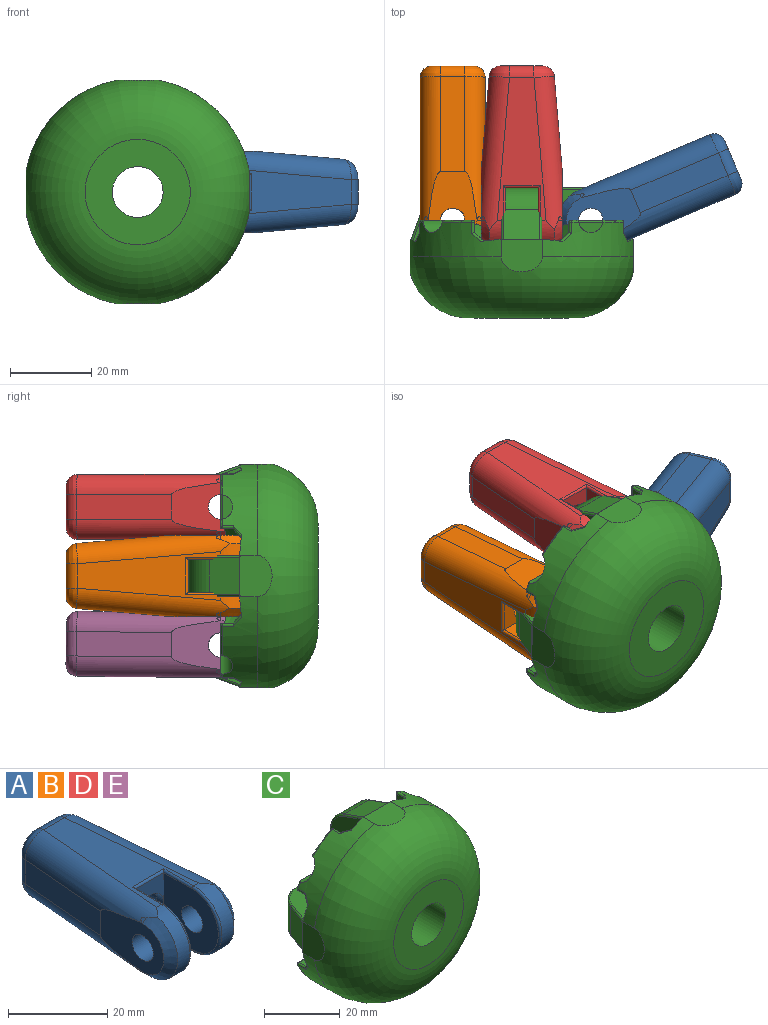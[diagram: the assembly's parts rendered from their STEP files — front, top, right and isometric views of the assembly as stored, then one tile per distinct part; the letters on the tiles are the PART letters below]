
ASSEMBLY  parts=5 mates=4
PART A: 43 faces, bbox 22.4x46.7x17.3 mm
  f0: plane 35.2x12mm, normal (0,0,1), area 240mm2, adj f1,f4,f25,f27,f29,f32,f34,f35
  f1: cylinder r=8mm len=16mm, axis (-1,0,0), area 82mm2, adj f0,f2,f18,f23,f31,f34
  f2: plane 35.2x12mm, normal (0,0,-1), area 240mm2, adj f1,f4,f22,f24,f26,f31,f33,f42
  f3: cylinder r=3mm len=6mm, axis (-1,0,0), area 112.2mm2, adj f8,f10
  f4: cylinder r=8mm len=16mm, axis (-1,0,0), area 82mm2, adj f0,f2,f15,f28,f32,f33
  f5: plane 10.45x10.4mm, normal (0,1,0), area 22.8mm2, adj f20,f35,f36,f37,f38,f39,f40,f41
  f6: cylinder r=3mm len=6mm, axis (-1,0,0), area 112.2mm2, adj f7,f11
  f7: plane 18x12mm, normal (1,0,0), area 149.6mm2, adj f6,f12,f14,f15,f16,f32,f33
  f8: plane 18x12mm, normal (-1,0,0), area 149.6mm2, adj f3,f13,f17,f18,f19,f31,f34
  f9: plane 15x8.1mm, normal (0,-1,0), area 71.2mm2, adj f10,f11,f24,f27,f30
  f10: plane 15.5x15mm, normal (1,0,0), area 180.1mm2, adj f3,f9,f22,f23,f25
  f11: plane 15.5x15mm, normal (-1,0,0), area 180.1mm2, adj f6,f9,f26,f28,f29
  f12: plane 23.44x6mm, normal (1,0.08,0), area 141.1mm2, adj f7,f32,f33,f38
  f13: plane 23.44x6mm, normal (-1,0.08,0), area 141.1mm2, adj f8,f31,f34,f39
  f14: plane 1.02x1.02mm, normal (0.71,0,-0.71), area 1mm2, adj f7,f15,f33
  f15: cone r=6mm half-angle=45deg, axis (-1,0,0), area 58.7mm2, adj f4,f7,f14,f16,f32,f33
  f16: plane 1.02x1.02mm, normal (0.71,0,0.71), area 1mm2, adj f7,f15,f32
  f17: plane 1.02x1.02mm, normal (-0.71,0,-0.71), area 1mm2, adj f8,f18,f31
  f18: cone r=8mm half-angle=45deg, axis (1,0,0), area 58.7mm2, adj f1,f8,f17,f19,f31,f34
  f19: plane 1.02x1.02mm, normal (-0.71,0,0.71), area 1mm2, adj f8,f18,f34
  f20: cylinder r=5.1mm len=28mm, axis (0,1,0), area 897.2mm2, adj f5,f21
  f21: plane 10.2x10.2mm, normal (0,1,0), area 31.4mm2, adj f20,f30
  f22: cylinder r=0.5mm len=8.5mm, axis (0,1,0), area 6.4mm2, adj f2,f10,f23,f24
  f23: torus R=7.5mm, axis (1,0,0), area 19.3mm2, adj f1,f10,f22,f25
  f24: cylinder r=0.5mm len=9.1mm, axis (1,0,0), area 6.6mm2, adj f2,f9,f22,f26
  f25: cylinder r=0.5mm len=8.5mm, axis (0,-1,0), area 6.4mm2, adj f0,f10,f23,f27
  f26: cylinder r=0.5mm len=8.5mm, axis (0,-1,0), area 6.4mm2, adj f2,f11,f24,f28
  f27: cylinder r=0.5mm len=9.1mm, axis (-1,0,0), area 6.6mm2, adj f0,f9,f25,f29
  f28: torus R=7.5mm, axis (1,0,0), area 19.3mm2, adj f4,f11,f26,f29
  f29: cylinder r=0.5mm len=8.5mm, axis (0,1,0), area 6.4mm2, adj f0,f11,f27,f28
  f30: cylinder r=4mm len=8mm, axis (0,1,0), area 50.3mm2, adj f9,f21
  f31: cylinder r=5mm len=38.07mm, axis (0.08,1,0), area 255.8mm2, adj f1,f2,f8,f13,f17,f18,f41
  f32: cylinder r=5mm len=38.07mm, axis (-0.08,1,0), area 255.8mm2, adj f0,f4,f7,f12,f15,f16,f36
  f33: cylinder r=5mm len=38.07mm, axis (-0.08,1,0), area 255.8mm2, adj f2,f4,f7,f12,f14,f15,f40
  f34: cylinder r=5mm len=38.07mm, axis (0.08,1,0), area 255.8mm2, adj f0,f1,f8,f13,f18,f19,f37
  f35: cylinder r=2.8mm len=6.04mm, axis (1,0,0), area 26.6mm2, adj f0,f5,f36,f37
  f36: bspline ~5.88x5.22mm, area 26.4mm2, adj f5,f32,f35,f38
  f37: bspline ~5.87x5.23mm, area 26.4mm2, adj f5,f34,f35,f39
  f38: cylinder r=2.8mm len=6mm, axis (0,0,1), area 25mm2, adj f5,f12,f36,f40
  f39: cylinder r=2.8mm len=6mm, axis (0,0,1), area 25mm2, adj f5,f13,f37,f41
  f40: bspline ~5.87x5.23mm, area 26.4mm2, adj f5,f33,f38,f42
  f41: bspline ~5.88x5.22mm, area 26.4mm2, adj f5,f31,f39,f42
  f42: cylinder r=2.8mm len=6.04mm, axis (-1,0,0), area 26.6mm2, adj f2,f5,f40,f41
PART B: same geometry as A
PART C: 170 faces, bbox 58.4x35.2x58.6 mm
  f0: plane 12.55x1.9mm, normal (0,1,0), area 22.9mm2, adj f2,f113,f115,f169
  f1: cylinder r=0.5mm len=4.69mm, axis (1,0,0), area 3.7mm2, adj f54,f74,f114,f169
  f2: torus R=27.46mm, axis (0,-1,0), area 1.6mm2, adj f0,f19,f117,f169
  f3: plane 12.55x1.9mm, normal (0,1,0), area 22.9mm2, adj f4,f123,f125,f168
  f4: torus R=27.46mm, axis (0,-1,0), area 1.6mm2, adj f3,f28,f122,f168
  f5: cylinder r=0.5mm len=4.69mm, axis (0,0,-1), area 3.7mm2, adj f45,f75,f126,f168
  f6: plane 12.55x1.9mm, normal (0,1,0), area 22.9mm2, adj f96,f97,f98,f167
  f7: torus R=27.46mm, axis (0,-1,0), area 6.7mm2, adj f33,f76,f99,f167
  f8: cylinder r=0.5mm len=4.69mm, axis (-1,0,0), area 3.7mm2, adj f39,f76,f99,f167
  f9: plane 12.55x1.9mm, normal (0,1,0), area 22.9mm2, adj f104,f106,f107,f166
  f10: cylinder r=0.5mm len=4.69mm, axis (0,0,1), area 3.7mm2, adj f63,f73,f105,f166
  f11: torus R=27.46mm, axis (0,-1,0), area 6.7mm2, adj f20,f73,f105,f166
  f12: plane 7.75x5.04mm, normal (0,0.94,0.34), area 28.4mm2, adj f27,f28,f77,f128,f146,f147
  f13: plane 7.57x4.05mm, normal (0,0.01,1), area 30.4mm2, adj f15,f24,f71,f135,f137
  f14: plane 20.38x7.85mm, normal (0,0.94,-0.34), area 67.6mm2, adj f15,f19,f20,f21,f65,f68,f70,f71
  f15: cylinder r=8mm len=10.74mm, axis (-1,0,0), area 63.4mm2, adj f13,f14,f23,f71,f87
  f16: plane 7.57x4.05mm, normal (1,0.01,0), area 30.4mm2, adj f17,f62,f66,f140,f141
  f17: cylinder r=8mm len=10.74mm, axis (0,0,1), area 63.4mm2, adj f16,f25,f62,f65,f83
  f18: plane 34x34mm, normal (0,1,0), area 466.8mm2, adj f37,f40,f49,f58,f67,f134,f135,f136
  f19: cylinder r=27.96mm len=22.45mm, axis (0,1,0), area 207.8mm2, adj f2,f14,f21,f25,f29,f72,f111,f112
  f20: cylinder r=27.96mm len=22.45mm, axis (0,1,0), area 207.8mm2, adj f11,f14,f21,f35,f36,f72,f102,f103
  f21: plane 10.1x8mm, normal (0,0,1), area 72.8mm2, adj f14,f19,f20,f72
  f22: plane 13.05x5mm, normal (0,0,-1), area 51.1mm2, adj f63,f85,f86,f106,f109,f110
  f23: cylinder r=8mm len=10.74mm, axis (0,0,-1), area 63.4mm2, adj f15,f24,f35,f43,f86
  f24: plane 7.57x4.05mm, normal (-1,0.01,0), area 30.4mm2, adj f13,f23,f43,f134,f136
  f25: plane 20.38x7.85mm, normal (-0.34,0.94,0), area 67.6mm2, adj f17,f19,f28,f29,f56,f59,f61,f62
  f26: plane 7.57x4.05mm, normal (0,0.01,-1), area 30.4mm2, adj f27,f53,f57,f150,f151
  f27: cylinder r=8mm len=10.74mm, axis (1,0,0), area 63.5mm2, adj f12,f26,f53,f56,f78,f129,f146
  f28: cylinder r=27.96mm len=22.45mm, axis (0,1,0), area 208.1mm2, adj f4,f12,f25,f29,f34,f72,f120,f121
  f29: plane 10.1x8mm, normal (1,0,0), area 72.8mm2, adj f19,f25,f28,f72
  f30: plane 14.04x7.85mm, normal (0,0.94,0.34), area 34.8mm2, adj f33,f34,f47,f50,f52,f92,f93,f147
  f31: plane 7.57x4.05mm, normal (-1,0.01,0), area 30.4mm2, adj f32,f44,f48,f158,f159
  f32: cylinder r=8mm len=10.74mm, axis (0,0,-1), area 63.4mm2, adj f31,f35,f44,f47,f90
  f33: cylinder r=27.96mm len=22.45mm, axis (0,1,0), area 207.8mm2, adj f7,f30,f34,f35,f36,f72,f93,f94
  f34: plane 12.6x10.55mm, normal (0,0,-1), area 72.8mm2, adj f28,f30,f33,f72,f147
  f35: plane 20.38x7.85mm, normal (0.34,0.94,0), area 67.6mm2, adj f20,f23,f32,f33,f36,f41,f43,f44
  f36: plane 10.1x8mm, normal (-1,0,0), area 72.8mm2, adj f20,f33,f35,f72
  f37: cylinder r=6.25mm len=32mm, axis (0,1,0), area 1256.6mm2, adj f18,f38
  f38: plane 25.92x25.92mm, normal (0,-1,0), area 404.9mm2, adj f37,f72
  f39: plane 13.05x5mm, normal (0,0,1), area 39.9mm2, adj f8,f46,f89,f90,f98,f100,f101,f167
  f40: cylinder r=8mm len=8.9mm, axis (0,0,-1), area 87mm2, adj f18,f41,f132,f157
  f41: plane 8.9x7.52mm, normal (-0.94,0.34,0), area 71.2mm2, adj f35,f40,f130,f156
  f42: cylinder r=3mm len=9.9mm, axis (0,0,-1), area 186.6mm2, adj f43,f44
  f43: plane 17.85x15.5mm, normal (0,0,1), area 187.8mm2, adj f23,f24,f35,f42,f130,f132,f134
  f44: plane 17.85x15.5mm, normal (0,0,-1), area 187.8mm2, adj f31,f32,f35,f42,f156,f157,f158
  f45: plane 12.58x5.03mm, normal (-1,0,0), area 39.2mm2, adj f5,f77,f78,f125,f127,f128,f129,f164
  f46: plane 13.05x5mm, normal (1,0,0), area 51.1mm2, adj f39,f91,f92,f93,f94,f96
  f47: cylinder r=8mm len=10.74mm, axis (1,0,0), area 63.4mm2, adj f30,f32,f48,f52,f91
  f48: plane 7.57x4.05mm, normal (0,0.01,-1), area 30.4mm2, adj f31,f47,f52,f160,f161
  f49: cylinder r=8mm len=8.9mm, axis (1,0,0), area 87mm2, adj f18,f50,f149,f163
  f50: plane 8.9x7.52mm, normal (0,0.34,-0.94), area 71.1mm2, adj f30,f49,f147,f148,f162
  f51: cylinder r=3mm len=9.9mm, axis (1,0,0), area 186.6mm2, adj f52,f53
  f52: plane 17.85x15.5mm, normal (-1,0,0), area 187.8mm2, adj f30,f47,f48,f51,f161,f162,f163
  f53: plane 17.68x15.5mm, normal (1,0,0), area 183.1mm2, adj f26,f27,f51,f146,f148,f149,f150
  f54: plane 13.05x5mm, normal (0,0,-1), area 39.9mm2, adj f1,f64,f83,f84,f111,f112,f113,f169
  f55: plane 12.58x5.03mm, normal (0,0,1), area 50.4mm2, adj f79,f80,f120,f121,f123,f129,f164
  f56: cylinder r=8mm len=10.74mm, axis (0,0,1), area 64.2mm2, adj f25,f27,f57,f61,f79,f129
  f57: plane 7.57x4.05mm, normal (1,0.01,0), area 30.4mm2, adj f26,f56,f61,f152,f153
  f58: cylinder r=8mm len=8.9mm, axis (0,0,1), area 87mm2, adj f18,f59,f139,f155
  f59: plane 8.9x7.52mm, normal (0.94,0.34,0), area 71.2mm2, adj f25,f58,f138,f154
  f60: cylinder r=3mm len=9.9mm, axis (0,0,1), area 186.6mm2, adj f61,f62
  f61: plane 17.85x15.5mm, normal (0,0,-1), area 187.8mm2, adj f25,f56,f57,f60,f153,f154,f155
  f62: plane 17.85x15.5mm, normal (0,0,1), area 187.8mm2, adj f16,f17,f25,f60,f138,f139,f140
  f63: plane 13.05x5mm, normal (1,0,0), area 39.9mm2, adj f10,f22,f87,f88,f102,f103,f104,f166
  f64: plane 13.05x5mm, normal (-1,0,0), area 51.1mm2, adj f54,f81,f82,f115,f118,f119
  f65: cylinder r=8mm len=10.74mm, axis (-1,0,0), area 63.4mm2, adj f14,f17,f66,f70,f82
  f66: plane 7.57x4.05mm, normal (0,0.01,1), area 30.4mm2, adj f16,f65,f70,f142,f143
  f67: cylinder r=8mm len=8.9mm, axis (-1,0,0), area 87mm2, adj f18,f68,f133,f145
  f68: plane 8.9x7.52mm, normal (0,0.34,0.94), area 71.2mm2, adj f14,f67,f131,f144
  f69: cylinder r=3mm len=9.9mm, axis (-1,0,0), area 186.6mm2, adj f70,f71
  f70: plane 17.85x15.5mm, normal (1,0,0), area 187.8mm2, adj f14,f65,f66,f69,f143,f144,f145
  f71: plane 17.85x15.5mm, normal (-1,0,0), area 187.8mm2, adj f13,f14,f15,f69,f131,f133,f135
  f72: torus R=12.96mm, axis (0,-1,0), area 3224.7mm2, adj f19,f20,f21,f28,f29,f33,f34,f36
  f73: plane 6.72x4.65mm, normal (0,1,0), area 17.3mm2, adj f10,f11,f166
  f74: plane 6.72x4.65mm, normal (0,1,0), area 17.3mm2, adj f1,f116,f169
  f75: plane 6.72x4.65mm, normal (0,1,0), area 17.3mm2, adj f5,f124,f168
  f76: plane 6.72x4.65mm, normal (0,1,0), area 17.3mm2, adj f7,f8,f167
  f77: plane 6.78x4.43mm, normal (-0.71,0.66,0.24), area 22mm2, adj f12,f45,f78,f128
  f78: cone r=5.5mm half-angle=45deg, axis (-1,0,0), area 34.3mm2, adj f27,f45,f77,f129
  f79: cone r=8mm half-angle=45deg, axis (0,0,1), area 34.3mm2, adj f55,f56,f80,f129
  f80: plane 6.78x4.43mm, normal (-0.24,0.66,0.71), area 22mm2, adj f25,f55,f79,f120
  f81: plane 6.78x4.43mm, normal (-0.71,0.66,-0.24), area 22mm2, adj f14,f64,f82,f119
  f82: cone r=8mm half-angle=45deg, axis (-1,0,0), area 41.7mm2, adj f64,f65,f81,f83
  f83: cone r=5.5mm half-angle=45deg, axis (0,0,-1), area 41.7mm2, adj f17,f54,f82,f84
  f84: plane 6.78x4.43mm, normal (-0.24,0.66,-0.71), area 22mm2, adj f25,f54,f83,f111
  f85: plane 6.78x4.43mm, normal (0.24,0.66,-0.71), area 22mm2, adj f22,f35,f86,f110
  f86: cone r=8mm half-angle=45deg, axis (0,0,-1), area 41.7mm2, adj f22,f23,f85,f87
  f87: cone r=5.5mm half-angle=45deg, axis (1,0,0), area 41.7mm2, adj f15,f63,f86,f88
  f88: plane 6.78x4.43mm, normal (0.71,0.66,-0.24), area 22mm2, adj f14,f63,f87,f102
  f89: plane 6.78x4.43mm, normal (0.24,0.66,0.71), area 22mm2, adj f35,f39,f90,f101
  f90: cone r=5.5mm half-angle=45deg, axis (0,0,1), area 41.7mm2, adj f32,f39,f89,f91
  f91: cone r=8mm half-angle=45deg, axis (1,0,0), area 41.7mm2, adj f46,f47,f90,f92
  f92: plane 6.78x4.43mm, normal (0.71,0.66,0.24), area 22mm2, adj f30,f46,f91,f93
  f93: bspline ~9.25x8.44mm, area 3.5mm2, adj f30,f33,f46,f92,f94
  f94: cylinder r=0.5mm len=2.79mm, axis (0,1,0), area 2.7mm2, adj f33,f46,f93,f95
  f95: sphere r=0.5mm, area 0.5mm2, adj f94,f96,f97
  f96: cylinder r=0.5mm len=13.05mm, axis (0,0,1), area 10.1mm2, adj f6,f46,f95,f98
  f97: torus R=27.46mm, axis (0,-1,0), area 1.6mm2, adj f6,f33,f95,f167
  f98: cylinder r=0.5mm len=2.44mm, axis (-1,0,0), area 1.7mm2, adj f6,f39,f96,f167
  f99: sphere r=0.5mm, area 0.6mm2, adj f7,f8,f100
  f100: cylinder r=0.5mm len=2.79mm, axis (0,1,0), area 2.7mm2, adj f33,f39,f99,f101
  f101: bspline ~9.25x8.44mm, area 3.5mm2, adj f33,f35,f39,f89,f100
  f102: bspline ~9.25x8.44mm, area 3.5mm2, adj f14,f20,f63,f88,f103
  f103: cylinder r=0.5mm len=2.79mm, axis (0,1,0), area 2.7mm2, adj f20,f63,f102,f105
  f104: cylinder r=0.5mm len=2.44mm, axis (0,0,1), area 1.7mm2, adj f9,f63,f106,f166
  f105: sphere r=0.5mm, area 0.5mm2, adj f10,f11,f103
  f106: cylinder r=0.5mm len=13.05mm, axis (1,0,0), area 10.1mm2, adj f9,f22,f104,f108
  f107: torus R=27.46mm, axis (0,-1,0), area 1.6mm2, adj f9,f20,f108,f166
  f108: sphere r=0.5mm, area 0.6mm2, adj f106,f107,f109
  f109: cylinder r=0.5mm len=2.79mm, axis (0,1,0), area 2.7mm2, adj f20,f22,f108,f110
  f110: bspline ~9.25x8.44mm, area 3.5mm2, adj f20,f22,f35,f85,f109
  f111: bspline ~9.25x8.44mm, area 3.5mm2, adj f19,f25,f54,f84,f112
  f112: cylinder r=0.5mm len=2.79mm, axis (0,1,0), area 2.7mm2, adj f19,f54,f111,f114
  f113: cylinder r=0.5mm len=2.44mm, axis (1,0,0), area 1.7mm2, adj f0,f54,f115,f169
  f114: sphere r=0.5mm, area 0.3mm2, adj f1,f112,f116
  f115: cylinder r=0.5mm len=13.05mm, axis (0,0,-1), area 10.1mm2, adj f0,f64,f113,f117
  f116: torus R=27.46mm, axis (0,-1,0), area 6.7mm2, adj f19,f74,f114,f169
  f117: sphere r=0.5mm, area 0.5mm2, adj f2,f115,f118
  f118: cylinder r=0.5mm len=2.79mm, axis (0,1,0), area 2.7mm2, adj f19,f64,f117,f119
  f119: bspline ~9.25x8.44mm, area 3.5mm2, adj f14,f19,f64,f81,f118
  f120: bspline ~9.25x8.44mm, area 3.5mm2, adj f25,f28,f55,f80,f121
  f121: cylinder r=0.5mm len=2.79mm, axis (0,1,0), area 2.7mm2, adj f28,f55,f120,f122
  f122: sphere r=0.5mm, area 0.3mm2, adj f4,f121,f123
  f123: cylinder r=0.5mm len=12.55mm, axis (-1,0,0), area 9.9mm2, adj f3,f55,f122,f165
  f124: torus R=27.46mm, axis (0,-1,0), area 6.7mm2, adj f28,f75,f126,f168
  f125: cylinder r=0.5mm len=1.94mm, axis (0,0,-1), area 1.5mm2, adj f3,f45,f165,f168
  f126: sphere r=0.5mm, area 0.5mm2, adj f5,f124,f127
  f127: cylinder r=0.5mm len=2.79mm, axis (0,1,0), area 2.7mm2, adj f28,f45,f126,f128
  f128: bspline ~9.25x8.44mm, area 3.5mm2, adj f12,f28,f45,f77,f127
  f129: bspline ~4.62x4.62mm, area 4.1mm2, adj f27,f45,f55,f56,f78,f79,f164
  f130: cylinder r=0.5mm len=7.69mm, axis (0.34,0.94,0), area 6.3mm2, adj f35,f41,f43,f132
  f131: cylinder r=0.5mm len=7.69mm, axis (0,-0.94,0.34), area 6.3mm2, adj f14,f68,f71,f133
  f132: torus R=7.5mm, axis (0,0,1), area 7.5mm2, adj f40,f43,f130,f134
  f133: torus R=7.5mm, axis (1,0,0), area 7.5mm2, adj f67,f71,f131,f135
  f134: cylinder r=0.5mm len=8.57mm, axis (1,0,0), area 6.5mm2, adj f18,f24,f43,f132,f136
  f135: cylinder r=0.5mm len=8.57mm, axis (0,0,1), area 6.5mm2, adj f13,f18,f71,f133,f137
  f136: cylinder r=0.5mm len=4.48mm, axis (0,0,1), area 3.1mm2, adj f18,f24,f134,f137
  f137: cylinder r=0.5mm len=4.48mm, axis (1,0,0), area 3.1mm2, adj f13,f18,f135,f136
  f138: cylinder r=0.5mm len=7.69mm, axis (0.34,-0.94,0), area 6.3mm2, adj f25,f59,f62,f139
  f139: torus R=7.5mm, axis (0,0,-1), area 7.5mm2, adj f58,f62,f138,f140
  f140: cylinder r=0.5mm len=8.57mm, axis (1,0,0), area 6.5mm2, adj f16,f18,f62,f139,f141
  f141: cylinder r=0.5mm len=4.48mm, axis (0,0,-1), area 3.1mm2, adj f16,f18,f140,f142
  f142: cylinder r=0.5mm len=4.48mm, axis (1,0,0), area 3.1mm2, adj f18,f66,f141,f143
  f143: cylinder r=0.5mm len=8.57mm, axis (0,0,-1), area 6.5mm2, adj f18,f66,f70,f142,f145
  f144: cylinder r=0.5mm len=7.69mm, axis (0,0.94,-0.34), area 6.3mm2, adj f14,f68,f70,f145
  f145: torus R=7.5mm, axis (1,0,0), area 7.5mm2, adj f67,f70,f143,f144
  f146: cylinder r=0.5mm len=9.83mm, axis (0,-0.34,0.94), area 7mm2, adj f12,f27,f53,f147
  f147: torus R=1mm, axis (0,0.94,0.34), area 1mm2, adj f12,f28,f30,f34,f50,f146,f148
  f148: cylinder r=0.5mm len=7.22mm, axis (0,-0.94,-0.34), area 5.9mm2, adj f50,f53,f147,f149
  f149: torus R=7.5mm, axis (-1,0,0), area 7.5mm2, adj f49,f53,f148,f150
  f150: cylinder r=0.5mm len=8.57mm, axis (0,0,-1), area 6.5mm2, adj f18,f26,f53,f149,f151
  f151: cylinder r=0.5mm len=4.48mm, axis (-1,0,0), area 3.1mm2, adj f18,f26,f150,f152
  f152: cylinder r=0.5mm len=4.48mm, axis (0,0,-1), area 3.1mm2, adj f18,f57,f151,f153
  f153: cylinder r=0.5mm len=8.57mm, axis (-1,0,0), area 6.5mm2, adj f18,f57,f61,f152,f155
  f154: cylinder r=0.5mm len=7.69mm, axis (-0.34,0.94,0), area 6.3mm2, adj f25,f59,f61,f155
  f155: torus R=7.5mm, axis (0,0,-1), area 7.5mm2, adj f58,f61,f153,f154
  f156: cylinder r=0.5mm len=7.69mm, axis (-0.34,-0.94,0), area 6.3mm2, adj f35,f41,f44,f157
  f157: torus R=7.5mm, axis (0,0,1), area 7.5mm2, adj f40,f44,f156,f158
  f158: cylinder r=0.5mm len=8.57mm, axis (-1,0,0), area 6.5mm2, adj f18,f31,f44,f157,f159
  f159: cylinder r=0.5mm len=4.48mm, axis (0,0,1), area 3.1mm2, adj f18,f31,f158,f160
  f160: cylinder r=0.5mm len=4.48mm, axis (-1,0,0), area 3.1mm2, adj f18,f48,f159,f161
  f161: cylinder r=0.5mm len=8.57mm, axis (0,0,1), area 6.5mm2, adj f18,f48,f52,f160,f163
  f162: cylinder r=0.5mm len=7.69mm, axis (0,0.94,0.34), area 6.3mm2, adj f30,f50,f52,f163
  f163: torus R=7.5mm, axis (-1,0,0), area 7.5mm2, adj f49,f52,f161,f162
  f164: cylinder r=0.5mm len=2.13mm, axis (0,1,0), area 1.7mm2, adj f45,f55,f129,f165
  f165: sphere r=0.5mm, area 0.5mm2, adj f123,f125,f164
  f166: cylinder r=3mm len=12.58mm, axis (1,0,0), area 97.8mm2, adj f9,f10,f11,f20,f63,f73,f104,f107
  f167: cylinder r=3mm len=12.58mm, axis (0,0,1), area 97.8mm2, adj f6,f7,f8,f33,f39,f76,f97,f98
  f168: cylinder r=3mm len=12.58mm, axis (-1,0,0), area 97.8mm2, adj f3,f4,f5,f28,f45,f75,f124,f125
  f169: cylinder r=3mm len=12.58mm, axis (0,0,-1), area 97.8mm2, adj f0,f1,f2,f19,f54,f74,f113,f116
PART D: same geometry as A
PART E: same geometry as A
PLACE A rot(axis=(-0.48,-0.73,-0.48),107.7deg) t=(30.62,-19.6,0)mm
PLACE B rot(axis=(0,1,0),90deg) t=(-33,0,0)mm
PLACE C at identity fixed
PLACE D t=(0,0,1)mm
PLACE E rot(axis=(1,0,0),0.5deg) t=(0,0.14,-32.93)mm
MATE revolute C.f166 <-> D.f1  axis (-1,0,0) through (0,-8,17)mm
MATE revolute C.f149 <-> E.f1  axis (1,0,0) through (0,-8,-17)mm
MATE revolute C.f139 <-> A.f1  axis (0,0,1) through (17,-8,0)mm
MATE revolute C.f23 <-> B.f1  axis (0,0,-1) through (-17,-8,0)mm
